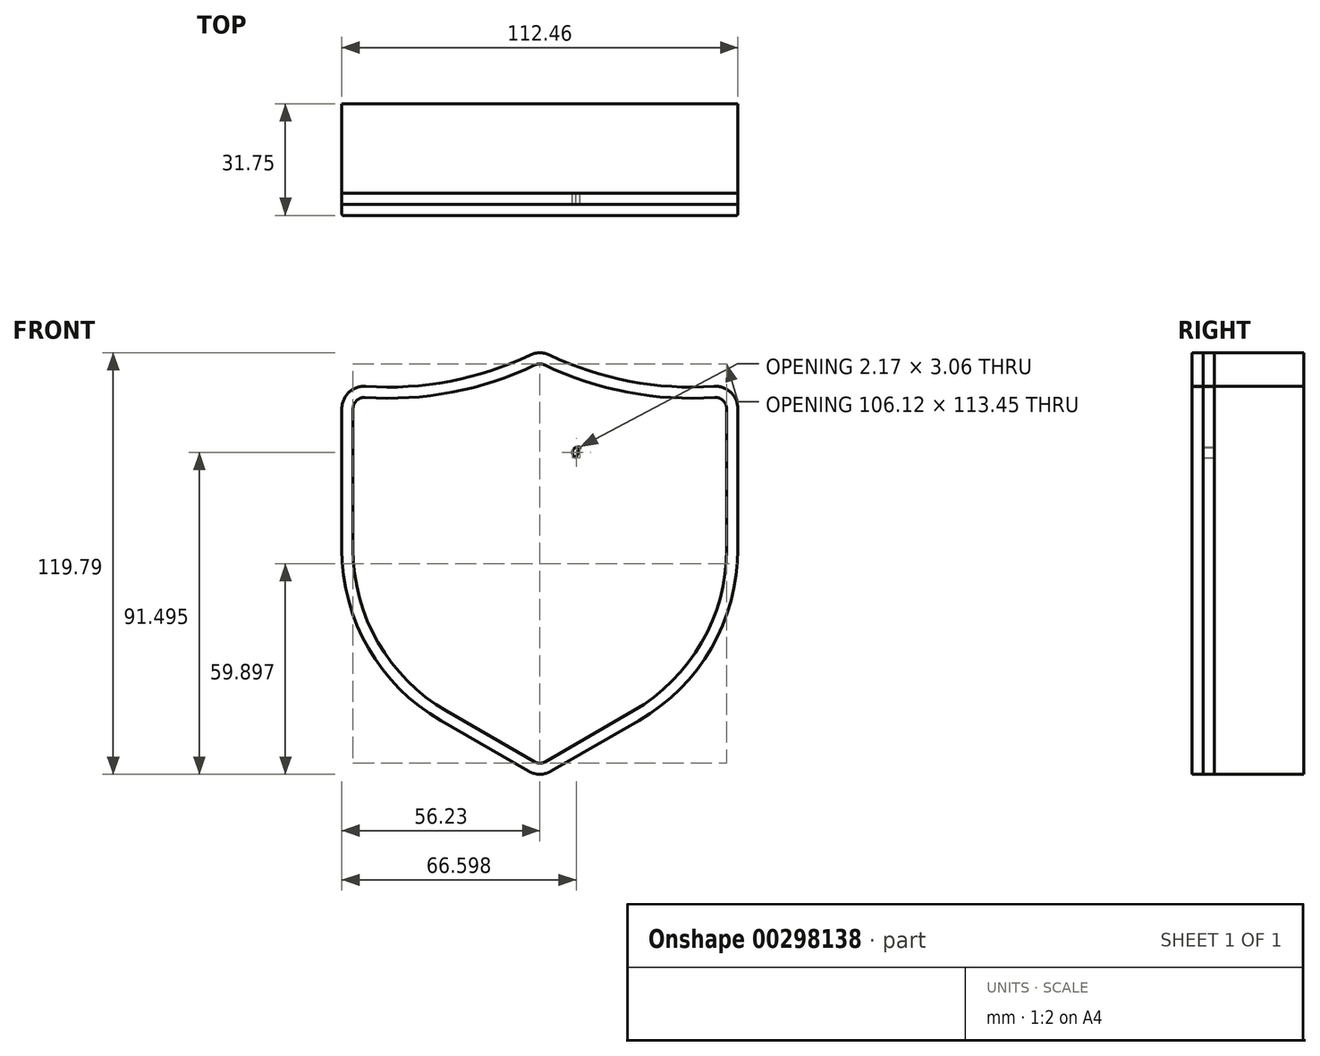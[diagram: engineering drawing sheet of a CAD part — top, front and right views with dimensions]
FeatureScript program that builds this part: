
annotation { "Feature Type Name" : "Feature", "Feature Type Description" : "" }
export const myFeature = defineFeature(function(context is Context, id is Id, definition is map)
    precondition{}
    {
        {
            var Q0;
            Q0=qCreatedBy(makeId("Front.planeOp"),FACE);
            var sketch = newSketch(context, id + "F0", { "sketchPlane" : qUnion([Q0])});
            skLineSegment(sketch, "E0", {"start": v(-56.23, 39.95) * mm, "end": v(-56.23, 0) * mm});
            skArc(sketch, "E1", {"start": v(-56.23, 0) * mm, "mid": v(-48.7, -28.12) * mm, "end": v(-28.12, -48.7) * mm});
            skLineSegment(sketch, "E2", {"start": v(-3.17, -63.1) * mm, "end": v(-28.12, -48.7) * mm});
            skArc(sketch, "E3", {"start": v(-49.45, 46.29) * mm, "mid": v(-25.52, 47.74) * mm, "end": v(-2.74, 55.22) * mm});
            skArc(sketch, "E4.MirrorCS", {"start": v(49.45, 46.29) * mm, "mid": v(25.52, 47.74) * mm, "end": v(2.74, 55.22) * mm});
            skLineSegment(sketch, "E5.MirrorCS", {"start": v(56.23, 39.95) * mm, "end": v(56.23, 0) * mm});
            skArc(sketch, "E6.MirrorCS", {"start": v(56.23, 0) * mm, "mid": v(48.7, -28.12) * mm, "end": v(28.12, -48.7) * mm});
            skLineSegment(sketch, "E7.MirrorCS", {"start": v(3.17, -63.1) * mm, "end": v(28.12, -48.7) * mm});
            skPoint(sketch, "E8.visualSharp", {"position": v(-56.23, 47) * mm});
            skArc(sketch, "E8.filletArc", {"start": v(-49.45, 46.29) * mm, "mid": v(-54.22, 44.6) * mm, "end": v(-56.23, 39.95) * mm});
            skPoint(sketch, "E9.visualSharp", {"position": v(0, 56.59) * mm});
            skArc(sketch, "E9.filletArc", {"start": v(2.74, 55.22) * mm, "mid": v(0, 55.84) * mm, "end": v(-2.74, 55.22) * mm});
            skPoint(sketch, "E10.visualSharp", {"position": v(56.23, 47) * mm});
            skArc(sketch, "E10.filletArc", {"start": v(56.23, 39.95) * mm, "mid": v(54.22, 44.6) * mm, "end": v(49.45, 46.29) * mm});
            skPoint(sketch, "E11.visualSharp", {"position": v(0, -64.93) * mm});
            skArc(sketch, "E11.filletArc", {"start": v(-3.17, -63.1) * mm, "mid": v(0, -63.95) * mm, "end": v(3.17, -63.1) * mm});
            skSolve(sketch);
        }
        {
            var Q0;
            Q0 = qSketchRegion(id + "F0", true);
            extrude(context, id + "F1", {"entities" : qUnion([Q0]), "oppositeDirection" : true, "depth" : 25.4 * mm});
        }
        {
            var Q0;
            Q0=makeQuery(id+"F1.opExtrude","CAP_FACE",FACE,{"disambiguationData":[OSD([sQuery(id+"F0.wireOp",EDGE,"E0"),sQuery(id+"F0.wireOp",EDGE,"E1"),sQuery(id+"F0.wireOp",EDGE,"E2"),sQuery(id+"F0.wireOp",EDGE,"E3"),sQuery(id+"F0.wireOp",EDGE,"E4.MirrorCS"),sQuery(id+"F0.wireOp",EDGE,"E5.MirrorCS"),sQuery(id+"F0.wireOp",EDGE,"E6.MirrorCS"),sQuery(id+"F0.wireOp",EDGE,"E7.MirrorCS"),sQuery(id+"F0.wireOp",EDGE,"E8.filletArc"),sQuery(id+"F0.wireOp",EDGE,"E9.filletArc"),sQuery(id+"F0.wireOp",EDGE,"E10.filletArc"),sQuery(id+"F0.wireOp",EDGE,"E11.filletArc")])],"isStart":true});
            var sketch = newSketch(context, id + "F2", { "sketchPlane" : qUnion([Q0])});
            skArc(sketch, "E12.0", {"start": v(-49.67, 43.12) * mm, "mid": v(-24.92, 44.62) * mm, "end": v(-1.37, 52.36) * mm});
            skArc(sketch, "E13.0", {"start": v(26.53, -45.95) * mm, "mid": v(45.95, -26.53) * mm, "end": v(53.06, 0) * mm});
            skLineSegment(sketch, "E13.1", {"start": v(1.59, -60.35) * mm, "end": v(26.53, -45.95) * mm});
            skLineSegment(sketch, "E13.2", {"start": v(53.06, 0) * mm, "end": v(53.06, 39.95) * mm});
            skLineSegment(sketch, "E13.3", {"start": v(-26.53, -45.95) * mm, "end": v(-1.59, -60.35) * mm});
            skArc(sketch, "E13.4", {"start": v(49.67, 43.12) * mm, "mid": v(24.92, 44.62) * mm, "end": v(1.37, 52.36) * mm});
            skArc(sketch, "E13.5", {"start": v(-1.37, 52.36) * mm, "mid": v(-24.92, 44.62) * mm, "end": v(-49.67, 43.12) * mm});
            skLineSegment(sketch, "E13.6", {"start": v(-53.06, 39.95) * mm, "end": v(-53.06, 0) * mm});
            skArc(sketch, "E13.7", {"start": v(-53.06, 0) * mm, "mid": v(-45.95, -26.53) * mm, "end": v(-26.53, -45.95) * mm});
            skPoint(sketch, "E14.visualSharp", {"position": v(-53.06, 43.41) * mm});
            skArc(sketch, "E14.filletArc", {"start": v(-49.67, 43.12) * mm, "mid": v(-52.05, 42.27) * mm, "end": v(-53.06, 39.95) * mm});
            skPoint(sketch, "E15.visualSharp", {"position": v(0, 53.03) * mm});
            skArc(sketch, "E15.filletArc", {"start": v(1.37, 52.36) * mm, "mid": v(0, 52.67) * mm, "end": v(-1.37, 52.36) * mm});
            skPoint(sketch, "E16.visualSharp", {"position": v(53.06, 43.41) * mm});
            skArc(sketch, "E16.filletArc", {"start": v(53.06, 39.95) * mm, "mid": v(52.05, 42.27) * mm, "end": v(49.67, 43.12) * mm});
            skPoint(sketch, "E17.visualSharp", {"position": v(0, -61.27) * mm});
            skArc(sketch, "E17.filletArc", {"start": v(-1.59, -60.35) * mm, "mid": v(0, -60.78) * mm, "end": v(1.59, -60.35) * mm});
            skSolve(sketch);
        }
        {
            var Q0;
            Q0=makeQuery(id+"F2.imprint","IMPRINT",FACE,{"disambiguationData":[TD([[makeQuery(id+"F2.imprint","IMPRINT",EDGE,{"derivedFrom":sQuery(id+"F2.wireOp",EDGE,"E13.0")}),-1.0]])]});
            extrude(context, id + "F3", {"entities" : qUnion([Q0]), "depth" : 6.35 * mm});
        }
        {
            var Q0;
            Q0=makeQuery(id+"F1.opExtrude","CAP_FACE",FACE,{"disambiguationData":[OSD([sQuery(id+"F0.wireOp",EDGE,"E0"),sQuery(id+"F0.wireOp",EDGE,"E1"),sQuery(id+"F0.wireOp",EDGE,"E2"),sQuery(id+"F0.wireOp",EDGE,"E3"),sQuery(id+"F0.wireOp",EDGE,"E4.MirrorCS"),sQuery(id+"F0.wireOp",EDGE,"E5.MirrorCS"),sQuery(id+"F0.wireOp",EDGE,"E6.MirrorCS"),sQuery(id+"F0.wireOp",EDGE,"E7.MirrorCS"),sQuery(id+"F0.wireOp",EDGE,"E8.filletArc"),sQuery(id+"F0.wireOp",EDGE,"E9.filletArc"),sQuery(id+"F0.wireOp",EDGE,"E10.filletArc"),sQuery(id+"F0.wireOp",EDGE,"E11.filletArc")])],"isStart":true});
            var sketch = newSketch(context, id + "F4", { "sketchPlane" : qUnion([Q0])});
            skArc(sketch, "E18", {"start": v(-10.29, 26.01) * mm, "mid": v(0, -27.97) * mm, "end": v(10.29, 26.01) * mm});
            skArc(sketch, "E19.0", {"start": v(-11.45, 28.97) * mm, "mid": v(0, -31.15) * mm, "end": v(11.45, 28.97) * mm});
            skLineSegment(sketch, "E20", {"start": v(-2.2, 35.18) * mm, "end": v(-2.2, 12.8) * mm});
            skLineSegment(sketch, "E21.MirrorCS", {"start": v(2.2, 35.18) * mm, "end": v(2.2, 12.8) * mm});
            skCircle(sketch, "E22", {"center": v(0, 35.18) * mm, "radius": 2.2 * mm});
            skCircle(sketch, "E23", {"center": v(0, 12.8) * mm, "radius": 2.2 * mm});
            skLineSegment(sketch, "E24", {"start": v(-10.29, 26.01) * mm, "end": v(-11.45, 28.97) * mm});
            skArc(sketch, "E25", {"start": v(-10.29, 26.01) * mm, "mid": v(-9.4, 28.07) * mm, "end": v(-11.45, 28.97) * mm});
            skArc(sketch, "E26.MirrorC", {"start": v(10.29, 26.01) * mm, "mid": v(9.4, 28.07) * mm, "end": v(11.45, 28.97) * mm});
            skLineSegment(sketch, "E27.MirrorCS", {"start": v(10.29, 26.01) * mm, "end": v(11.45, 28.97) * mm});
            skSolve(sketch);
        }
        {
            var Q0;
            Q0=makeQuery(id+"F4.imprint","IMPRINT",FACE,{"disambiguationData":[TD([[makeQuery(id+"F4.imprint","IMPRINT",EDGE,{"derivedFrom":sQuery(id+"F4.wireOp",EDGE,"E18")}),-1.0]])]});
            var Q1;
            Q1=makeQuery(id+"F4.imprint","IMPRINT",FACE,{"disambiguationData":[TD([[makeQuery(id+"F4.imprint","IMPRINT",EDGE,{"derivedFrom":sQuery(id+"F4.wireOp",EDGE,"E24")}),-1.0]])]});
            var Q2;
            {var subQ0=sQuery(id+"F4.wireOp",EDGE,"E20");Q2=makeQuery(id+"F4.imprint","IMPRINT",FACE,{"disambiguationData":[TD([[makeQuery(id+"F4.imprint","IMPRINT",EDGE,{"derivedFrom":subQ0}),1.0]])]});}
            var Q3;
            {var subQ0=sQuery(id+"F4.wireOp",EDGE,"E22");var subQ1=makeQuery(id+"F4.imprint","INTERSECT",VERTEX,{"derivedFrom":[sQuery(id+"F4.wireOp",EDGE,"E20"),subQ0]});Q3=makeQuery(id+"F4.imprint","IMPRINT",FACE,{"disambiguationData":[TD([[makeQuery(id+"F4.imprint","IMPRINT",EDGE,{"disambiguationData":[TD([[subQ1,1.0]])],"derivedFrom":subQ0}),1.0]])]});}
            var Q4;
            Q4=makeQuery(id+"F4.imprint","IMPRINT",FACE,{"disambiguationData":[TD([[makeQuery(id+"F4.imprint","IMPRINT",EDGE,{"derivedFrom":sQuery(id+"F4.wireOp",EDGE,"E26.MirrorC")}),-1.0]])]});
            var Q5;
            {var subQ0=sQuery(id+"F4.wireOp",EDGE,"E23");var subQ1=makeQuery(id+"F4.imprint","INTERSECT",VERTEX,{"derivedFrom":[sQuery(id+"F4.wireOp",EDGE,"E20"),subQ0]});Q5=makeQuery(id+"F4.imprint","IMPRINT",FACE,{"disambiguationData":[TD([[makeQuery(id+"F4.imprint","IMPRINT",EDGE,{"disambiguationData":[TD([[subQ1,1.0]])],"derivedFrom":subQ0}),1.0]])]});}
            extrude(context, id + "F5", {"entities" : qUnion([Q0, Q1, Q2, Q3, Q4, Q5]), "depth" : 3.17 * mm});
        }
        {
            var Q0;
            Q0=makeQuery(id+"F3.opExtrude","CAP_EDGE",EDGE,{"disambiguationData":[OSD([sQuery(id+"F0.wireOp",EDGE,"E3")])],"isStart":false});
            var Q1;
            Q1=makeQuery(id+"F3.opExtrude","CAP_EDGE",EDGE,{"disambiguationData":[OSD([sQuery(id+"F0.wireOp",EDGE,"E8.filletArc")])],"isStart":false});
            var Q2;
            Q2=makeQuery(id+"F3.opExtrude","CAP_EDGE",EDGE,{"disambiguationData":[OSD([sQuery(id+"F0.wireOp",EDGE,"E0")])],"isStart":false});
            var Q3;
            Q3=makeQuery(id+"F3.opExtrude","CAP_EDGE",EDGE,{"disambiguationData":[OSD([sQuery(id+"F2.wireOp",EDGE,"E13.5")])],"isStart":false});
            fillet(context, id + "F6", {"entities" : qUnion([Q0, Q1, Q2, Q3]), "radius" : 0.38 * mm, "tangentPropagation" : true, "allowEdgeOverflow" : false});
        }
    });
